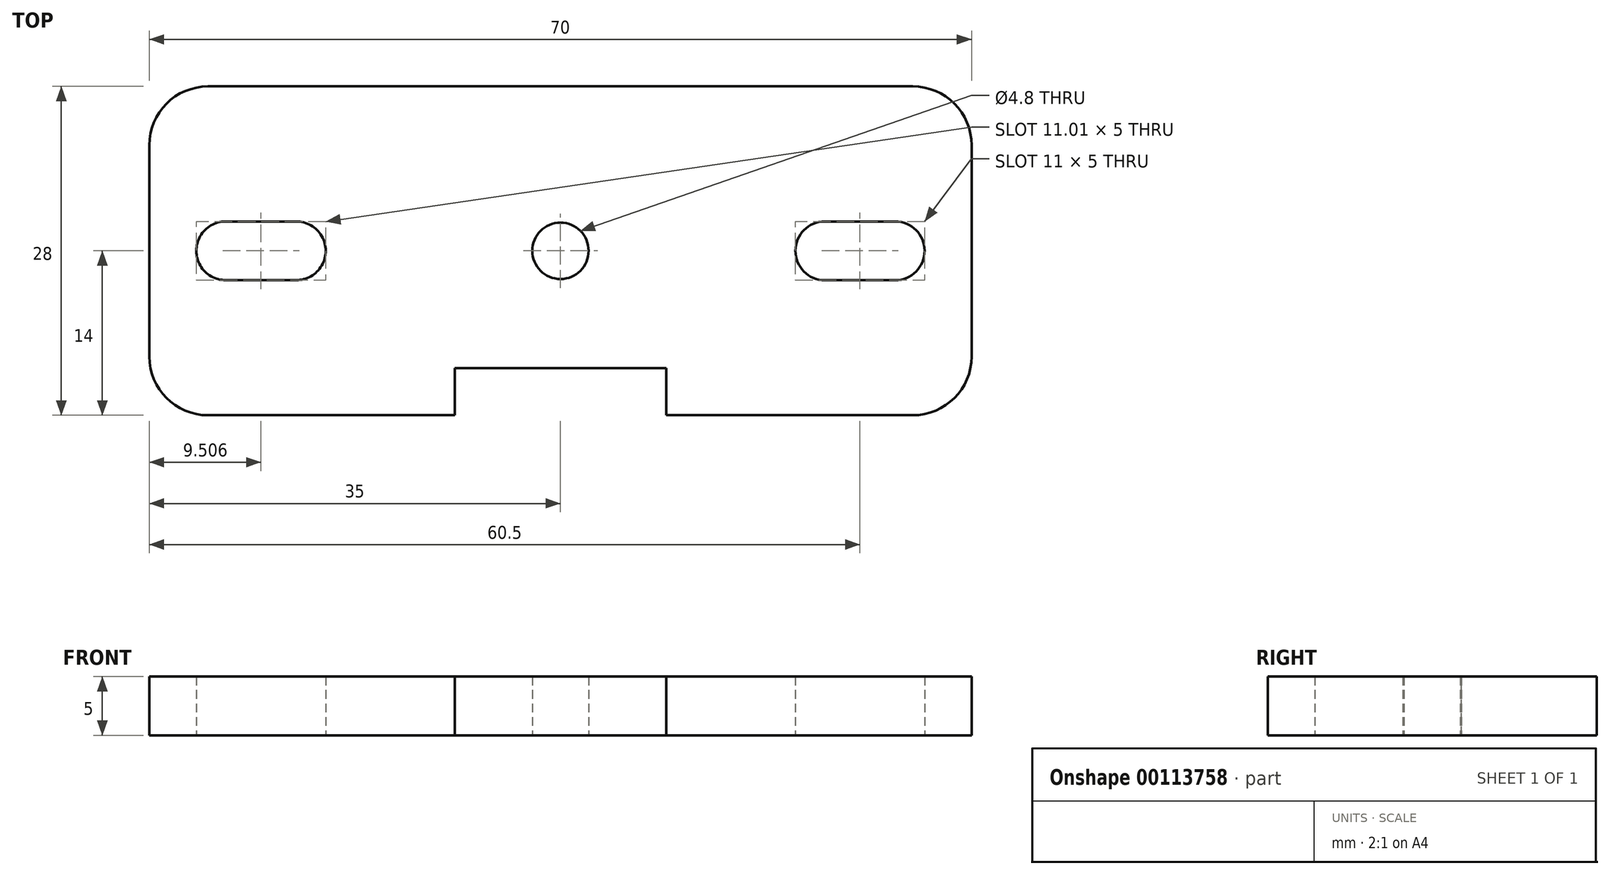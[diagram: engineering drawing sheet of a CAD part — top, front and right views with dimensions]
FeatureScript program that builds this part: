
annotation { "Feature Type Name" : "Feature", "Feature Type Description" : "" }
export const myFeature = defineFeature(function(context is Context, id is Id, definition is map)
    precondition{}
    {
        {
            var Q0;
            Q0=qCreatedBy(makeId("Top.planeOp"),FACE);
            var sketch = newSketch(context, id + "F0", { "sketchPlane" : qUnion([Q0])});
            skLineSegment(sketch, "E0.bottom", {"start": v(-30, 14) * mm, "end": v(30, 14) * mm});
            skLineSegment(sketch, "E0.top", {"start": v(-30, -14) * mm, "end": v(30, -14) * mm});
            skLineSegment(sketch, "E0.left", {"start": v(-35, 9) * mm, "end": v(-35, -9) * mm});
            skLineSegment(sketch, "E0.right", {"start": v(35, 9) * mm, "end": v(35, -9) * mm});
            skCircle(sketch, "E1", {"center": v(0, 0) * mm, "radius": 19 * mm});
            skLineSegment(sketch, "E2.bottom", {"start": v(-9, -14) * mm, "end": v(9, -14) * mm});
            skLineSegment(sketch, "E2.top", {"start": v(-9, -10) * mm, "end": v(9, -10) * mm});
            skLineSegment(sketch, "E2.left", {"start": v(-9, -14) * mm, "end": v(-9, -10) * mm});
            skLineSegment(sketch, "E2.right", {"start": v(9, -14) * mm, "end": v(9, -10) * mm});
            skCircle(sketch, "E3", {"center": v(0, 0) * mm, "radius": 2.4 * mm});
            skCircle(sketch, "E4", {"center": v(22.5, 0) * mm, "radius": 2.5 * mm});
            skCircle(sketch, "E5", {"center": v(28.5, 0) * mm, "radius": 2.5 * mm});
            skLineSegment(sketch, "E6.bottom", {"start": v(22.5, 2.5) * mm, "end": v(28.5, 2.5) * mm});
            skLineSegment(sketch, "E6.top", {"start": v(22.5, -2.5) * mm, "end": v(28.5, -2.5) * mm});
            skLineSegment(sketch, "E6.left", {"start": v(22.5, 2.5) * mm, "end": v(22.5, -2.5) * mm});
            skLineSegment(sketch, "E6.right", {"start": v(28.5, 2.5) * mm, "end": v(28.5, -2.5) * mm});
            skCircle(sketch, "E7", {"center": v(-28.5, 0) * mm, "radius": 2.5 * mm});
            skCircle(sketch, "E8", {"center": v(-22.49, 0) * mm, "radius": 2.5 * mm});
            skLineSegment(sketch, "E9.bottom", {"start": v(-28.5, 2.5) * mm, "end": v(-22.5, 2.5) * mm});
            skLineSegment(sketch, "E9.top", {"start": v(-28.5, -2.5) * mm, "end": v(-22.5, -2.5) * mm});
            skLineSegment(sketch, "E9.left", {"start": v(-28.5, 2.5) * mm, "end": v(-28.5, -2.5) * mm});
            skLineSegment(sketch, "E9.right", {"start": v(-22.5, 2.5) * mm, "end": v(-22.5, -2.5) * mm});
            skPoint(sketch, "E10.visualSharp", {"position": v(-35, 14) * mm});
            skArc(sketch, "E10.filletArc", {"start": v(-30, 14) * mm, "mid": v(-33.54, 12.54) * mm, "end": v(-35, 9) * mm});
            skPoint(sketch, "E11.visualSharp", {"position": v(-35, -14) * mm});
            skArc(sketch, "E11.filletArc", {"start": v(-35, -9) * mm, "mid": v(-33.54, -12.54) * mm, "end": v(-30, -14) * mm});
            skPoint(sketch, "E12.visualSharp", {"position": v(35, 14) * mm});
            skArc(sketch, "E12.filletArc", {"start": v(35, 9) * mm, "mid": v(33.54, 12.54) * mm, "end": v(30, 14) * mm});
            skPoint(sketch, "E13.visualSharp", {"position": v(35, -14) * mm});
            skArc(sketch, "E13.filletArc", {"start": v(30, -14) * mm, "mid": v(33.54, -12.54) * mm, "end": v(35, -9) * mm});
            skFitSpline(sketch, "E14", {"points": [v(-9, -10) * mm, v(-12.85, -14) * mm], "startDerivative": vector(-3.85, -4) * mm, "endDerivative": vector(-3.85, -4) * mm});
            skFitSpline(sketch, "E15", {"points": [v(9, -10) * mm, v(12.85, -14) * mm], "startDerivative": vector(3.85, -4) * mm, "endDerivative": vector(3.85, -4) * mm});
            skSolve(sketch);
        }
        {
            var Q0;
            {var subQ5=sQuery(id+"F0.wireOp",EDGE,"E0.left");Q0=makeQuery(id+"F0.imprint","IMPRINT",FACE,{"disambiguationData":[TD([[makeQuery(id+"F0.imprint","IMPRINT",EDGE,{"derivedFrom":subQ5}),1.0]])]});}
            var Q1;
            Q1=makeQuery(id+"F0.imprint","IMPRINT",FACE,{"disambiguationData":[TD([[makeQuery(id+"F0.imprint","IMPRINT",EDGE,{"derivedFrom":sQuery(id+"F0.wireOp",EDGE,"E2.top")}),1.0]])]});
            var Q2;
            {var subQ0=sQuery(id+"F0.wireOp",EDGE,"E1");var subQ1=sQuery(id+"F0.wireOp",EDGE,"E0.bottom");var subQ2=makeQuery(id+"F0.imprint","INTERSECT",VERTEX,{"disambiguationData":[OD(0.0)],"derivedFrom":[subQ1,subQ0]});Q2=makeQuery(id+"F0.imprint","IMPRINT",FACE,{"disambiguationData":[TD([[makeQuery(id+"F0.imprint","IMPRINT",EDGE,{"disambiguationData":[TD([[subQ2,-1.0]])],"derivedFrom":subQ1}),1.0]])]});}
            var Q3;
            {var subQ5=sQuery(id+"F0.wireOp",EDGE,"E0.right");Q3=makeQuery(id+"F0.imprint","IMPRINT",FACE,{"disambiguationData":[TD([[makeQuery(id+"F0.imprint","IMPRINT",EDGE,{"derivedFrom":subQ5}),-1.0]])]});}
            var Q4;
            Q4=makeQuery(id+"F0.imprint","IMPRINT",FACE,{"disambiguationData":[TD([[makeQuery(id+"F0.imprint","IMPRINT",EDGE,{"derivedFrom":sQuery(id+"F0.wireOp",EDGE,"E2.bottom")}),1.0]])]});
            var Q5;
            {var subQ0=sQuery(id+"F0.wireOp",EDGE,"E2.left");Q5=makeQuery(id+"F0.imprint","IMPRINT",FACE,{"disambiguationData":[TD([[makeQuery(id+"F0.imprint","IMPRINT",EDGE,{"derivedFrom":subQ0}),1.0]])]});}
            var Q6;
            {var subQ0=sQuery(id+"F0.wireOp",EDGE,"E2.right");Q6=makeQuery(id+"F0.imprint","IMPRINT",FACE,{"disambiguationData":[TD([[makeQuery(id+"F0.imprint","IMPRINT",EDGE,{"derivedFrom":subQ0}),-1.0]])]});}
            extrude(context, id + "F1", {"entities" : qUnion([Q0, Q1, Q2, Q3, Q4, Q5, Q6]), "depth" : 5 * mm});
        }
    });
